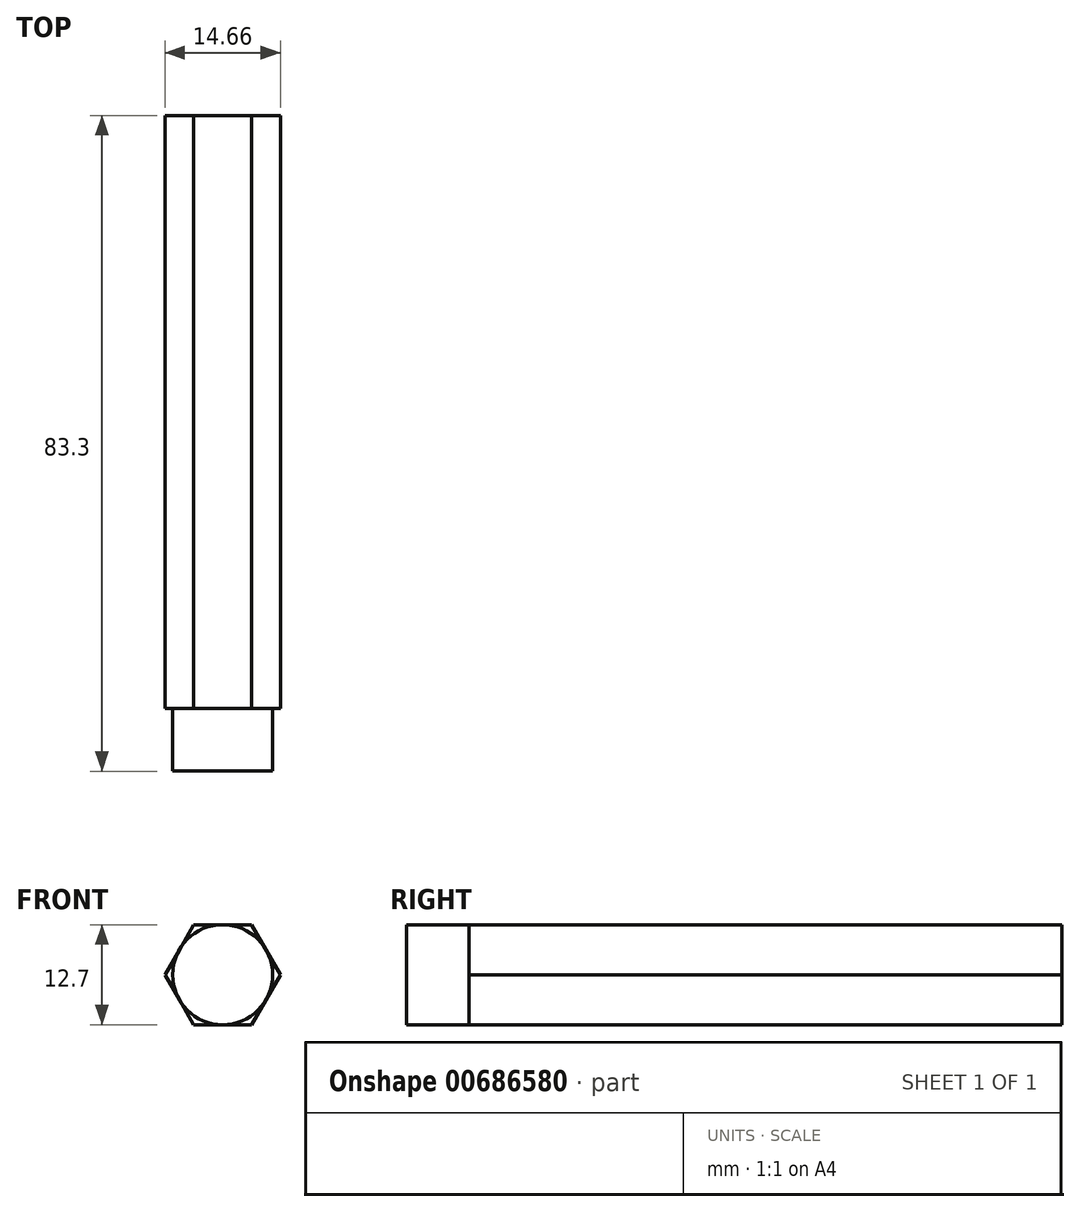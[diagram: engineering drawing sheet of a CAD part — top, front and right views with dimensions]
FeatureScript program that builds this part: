
annotation { "Feature Type Name" : "Feature", "Feature Type Description" : "" }
export const myFeature = defineFeature(function(context is Context, id is Id, definition is map)
    precondition{}
    {
        {
            var Q0;
            Q0=qCreatedBy(makeId("Front.planeOp"),FACE);
            var sketch = newSketch(context, id + "F0", { "sketchPlane" : qUnion([Q0])});
            skCircle(sketch, "E0.cCircle", {"center": v(0, 0) * mm, "radius": 6.35 * mm, "construction": true});
            skLineSegment(sketch, "E0.0", {"start": v(-3.67, 6.35) * mm, "end": v(3.67, 6.35) * mm});
            skLineSegment(sketch, "E0.1", {"start": v(3.67, 6.35) * mm, "end": v(7.33, 0) * mm});
            skLineSegment(sketch, "E0.2", {"start": v(7.33, 0) * mm, "end": v(3.67, -6.35) * mm});
            skLineSegment(sketch, "E0.3", {"start": v(3.67, -6.35) * mm, "end": v(-3.67, -6.35) * mm});
            skLineSegment(sketch, "E0.4", {"start": v(-3.67, -6.35) * mm, "end": v(-7.33, 0) * mm});
            skLineSegment(sketch, "E0.5", {"start": v(-7.33, 0) * mm, "end": v(-3.67, 6.35) * mm});
            skPoint(sketch, "E0.0.midPoint", {"position": v(0, 6.35) * mm});
            skSolve(sketch);
        }
        {
            var Q0;
            Q0 = qSketchRegion(id + "F0", true);
            extrude(context, id + "F1", {"entities" : qUnion([Q0]), "endBound" : BoundingType.SYMMETRIC, "depth" : 75.36 * mm, "offsetDistance" : 25.4 * mm});
        }
        {
            var Q0;
            Q0=makeQuery(id+"F1.opExtrude","CAP_FACE",FACE,{"disambiguationData":[OSD([sQuery(id+"F0.wireOp",EDGE,"E0.0"),sQuery(id+"F0.wireOp",EDGE,"E0.1"),sQuery(id+"F0.wireOp",EDGE,"E0.2"),sQuery(id+"F0.wireOp",EDGE,"E0.3"),sQuery(id+"F0.wireOp",EDGE,"E0.4"),sQuery(id+"F0.wireOp",EDGE,"E0.5")])],"isStart":false});
            var sketch = newSketch(context, id + "F2", { "sketchPlane" : qUnion([Q0])});
            skCircle(sketch, "E1", {"center": v(0, 0) * mm, "radius": 6.35 * mm});
            skSolve(sketch);
        }
        {
            var Q0;
            Q0 = qSketchRegion(id + "F2", true);
            extrude(context, id + "F3", {"entities" : qUnion([Q0]), "operationType" : NewBodyOperationType.ADD, "depth" : 7.94 * mm, "offsetDistance" : 25.4 * mm});
        }
    });
